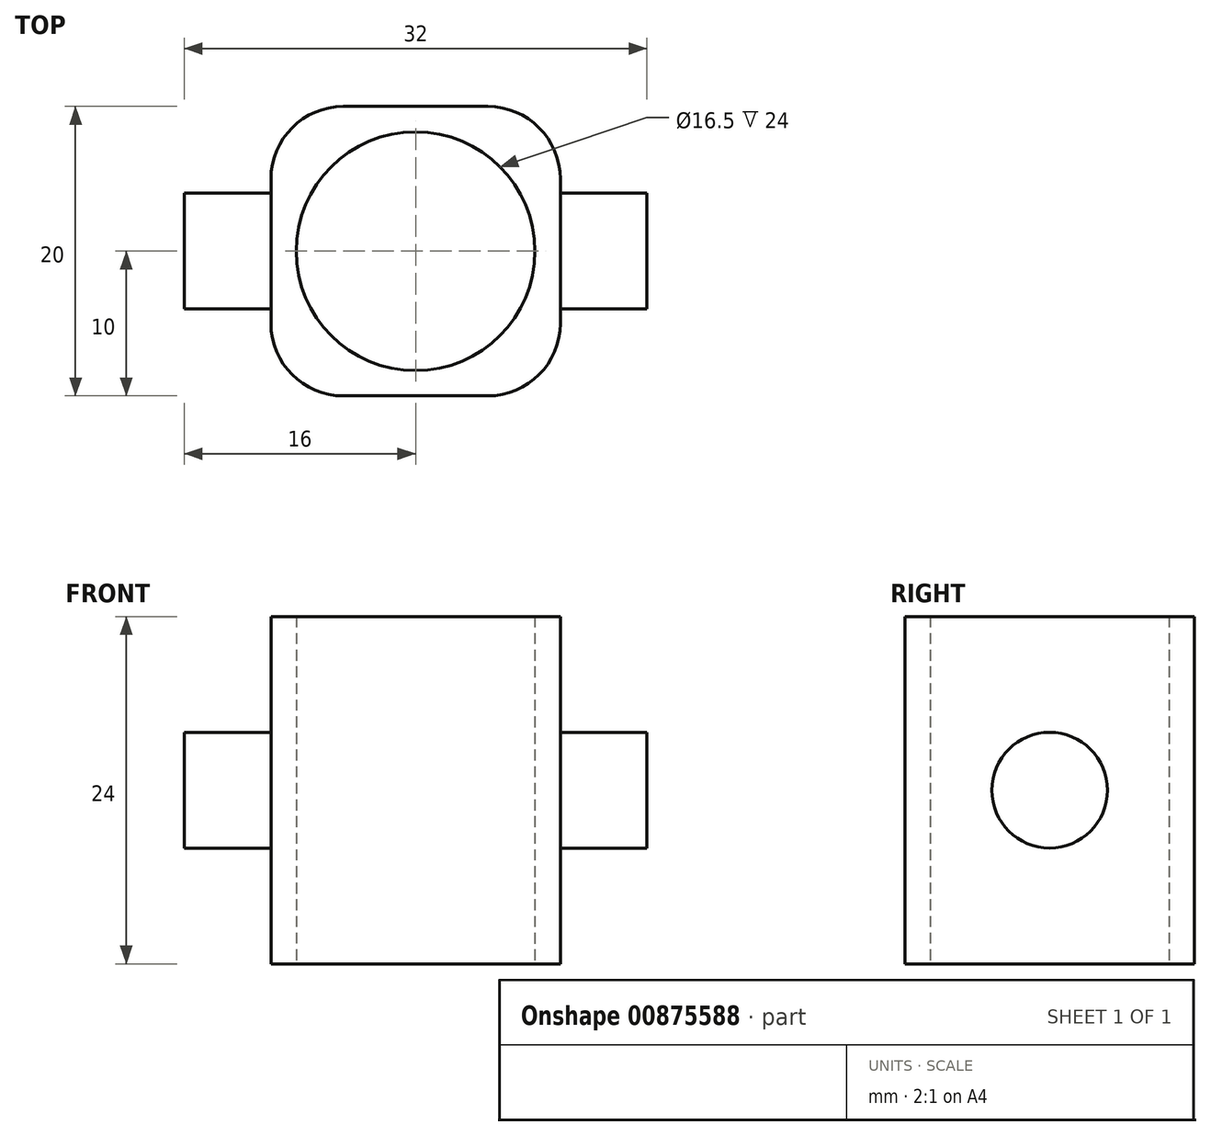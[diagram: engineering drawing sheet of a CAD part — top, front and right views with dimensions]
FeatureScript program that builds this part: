
annotation { "Feature Type Name" : "Feature", "Feature Type Description" : "" }
export const myFeature = defineFeature(function(context is Context, id is Id, definition is map)
    precondition{}
    {
        {
            var Q0;
            Q0=qCreatedBy(makeId("Top.planeOp"),FACE);
            var sketch = newSketch(context, id + "F0", { "sketchPlane" : qUnion([Q0])});
            skCircle(sketch, "E0", {"center": v(0, 0) * mm, "radius": 8.25 * mm});
            skLineSegment(sketch, "E1.bottom", {"start": v(10, 10) * mm, "end": v(-10, 10) * mm});
            skLineSegment(sketch, "E1.top", {"start": v(10, -10) * mm, "end": v(-10, -10) * mm});
            skLineSegment(sketch, "E1.left", {"start": v(10, 10) * mm, "end": v(10, -10) * mm});
            skLineSegment(sketch, "E1.right", {"start": v(-10, 10) * mm, "end": v(-10, -10) * mm});
            skSolve(sketch);
        }
        {
            var Q0;
            Q0=makeQuery(id+"F0.imprint","IMPRINT",FACE,{"disambiguationData":[TD([[makeQuery(id+"F0.imprint","IMPRINT",EDGE,{"derivedFrom":sQuery(id+"F0.wireOp",EDGE,"E0")}),-1.0]])]});
            extrude(context, id + "F1", {"entities" : qUnion([Q0]), "depth" : 24 * mm, "offsetDistance" : 25 * mm});
        }
        {
            var Q0;
            Q0=makeQuery(id+"F1.opExtrude","SWEPT_EDGE",EDGE,{"disambiguationData":[OSD([sQuery(id+"F0.wireOp",EDGE,"E1.bottom"),sQuery(id+"F0.wireOp",EDGE,"E1.left")])]});
            var Q1;
            Q1=makeQuery(id+"F1.opExtrude","SWEPT_EDGE",EDGE,{"disambiguationData":[OSD([sQuery(id+"F0.wireOp",EDGE,"E1.top"),sQuery(id+"F0.wireOp",EDGE,"E1.left")])]});
            var Q2;
            Q2=makeQuery(id+"F1.opExtrude","SWEPT_EDGE",EDGE,{"disambiguationData":[OSD([sQuery(id+"F0.wireOp",EDGE,"E1.bottom"),sQuery(id+"F0.wireOp",EDGE,"E1.right")])]});
            var Q3;
            Q3=makeQuery(id+"F1.opExtrude","SWEPT_EDGE",EDGE,{"disambiguationData":[OSD([sQuery(id+"F0.wireOp",EDGE,"E1.top"),sQuery(id+"F0.wireOp",EDGE,"E1.right")])]});
            fillet(context, id + "F2", {"entities" : qUnion([Q0, Q1, Q2, Q3]), "radius" : 5 * mm, "tangentPropagation" : true, "allowEdgeOverflow" : false});
        }
        {
            var Q0;
            Q0=makeQuery(id+"F1.opExtrude","SWEPT_FACE",FACE,{"disambiguationData":[OSD([sQuery(id+"F0.wireOp",EDGE,"E1.left")])]});
            var sketch = newSketch(context, id + "F3", { "sketchPlane" : qUnion([Q0])});
            skCircle(sketch, "E2", {"center": v(0, 12) * mm, "radius": 4 * mm});
            skPoint(sketch, "E2.centerSnap0", {"position": v(5, 12) * mm});
            skPoint(sketch, "E2.centerSnap1", {"position": v(0, 24) * mm});
            skSolve(sketch);
        }
        {
            var Q0;
            Q0=makeQuery(id+"F3.imprint","IMPRINT",FACE,{"disambiguationData":[TD([[makeQuery(id+"F3.imprint","IMPRINT",EDGE,{"derivedFrom":sQuery(id+"F3.wireOp",EDGE,"E2")}),1.0]])]});
            extrude(context, id + "F4", {"entities" : qUnion([Q0]), "operationType" : NewBodyOperationType.ADD, "depth" : 6 * mm, "offsetDistance" : 25 * mm});
        }
        {
            var Q0;
            Q0=makeQuery(id+"F1.opExtrude","SWEPT_FACE",FACE,{"disambiguationData":[OSD([sQuery(id+"F0.wireOp",EDGE,"E1.right")])]});
            var sketch = newSketch(context, id + "F5", { "sketchPlane" : qUnion([Q0])});
            skCircle(sketch, "E3", {"center": v(0, 12) * mm, "radius": 4 * mm});
            skPoint(sketch, "E3.centerSnap0", {"position": v(5, 12) * mm});
            skSolve(sketch);
        }
        {
            var Q0;
            Q0=makeQuery(id+"F5.imprint","IMPRINT",FACE,{"disambiguationData":[TD([[makeQuery(id+"F5.imprint","IMPRINT",EDGE,{"derivedFrom":sQuery(id+"F5.wireOp",EDGE,"E3")}),1.0]])]});
            extrude(context, id + "F6", {"entities" : qUnion([Q0]), "operationType" : NewBodyOperationType.ADD, "depth" : 6 * mm, "offsetDistance" : 25 * mm});
        }
    });
